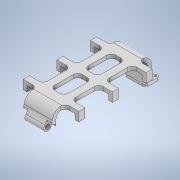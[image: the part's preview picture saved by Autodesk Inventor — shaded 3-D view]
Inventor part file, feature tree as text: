
AUTODESK INVENTOR PART (.ipt)
format: ipt  version: 2022 (Build 260153000, 153)  size: 560,640 bytes
history: native  units: mm
features: sketch x18, extrude x17, mirror x7, fillet x2, pattern_linear x1
ambient origin geometry x8: Origin, YZ Plane, XZ Plane, XY Plane, X Axis, Y Axis, Z Axis, Center Point
bodies: Solid1 (feature_tree)
feature tree (45):
  extrude  "Extrusion1"  Depth=15.4mm
  extrude  "Extrusion2"  Depth=1.5mm
  extrude  "Extrusion3"  Depth=6.0mm
  mirror  "Mirror1"
  mirror  "Mirror2"
  extrude  "Extrusion4"  Depth=1.0mm
  extrude  "Extrusion5"  Depth=3.0mm
  extrude  "Extrusion6"  Depth=16.0mm
  extrude  "Extrusion7"  Depth=3.0mm
  extrude  "Extrusion8"  Depth=1.0mm
  extrude  "Extrusion9"  Depth=1.0mm TaperAngle=0.0deg
  mirror  "Mirror4"
  extrude  "Extrusion11"  Depth=4.0mm TaperAngle=0.0deg
  extrude  "Extrusion12"  Depth=3.0mm
  mirror  "Mirror5"
  mirror  "Mirror6"
  pattern_linear  "Rectangular Pattern1"  Spacing1=2.0mm  [1 undecoded]
  extrude  "Extrusion13"  Depth=1.0mm
  extrude  "Extrusion14"  Depth=1.0mm
  extrude  "Extrusion15"  Depth=1.0mm
  mirror  "Mirror7"
  sketch  "Sketch16"  dims[d38=6.0mm]
  extrude  "Extrusion16"  Depth=1.0mm
  extrude  "Extrusion17"  TaperAngle=0.0deg  [1 undecoded]
  extrude  "Extrusion18"  Depth=2.5mm
  mirror  "Mirror8"
  fillet  "Fillet1"  Radius=12.5mm
  fillet  "Fillet2"  Radius=15.0mm
  sketch  "Sketch1"  dims[d0=36.5mm d1=15.4mm d2=7.7mm]
  sketch  "Sketch2"  dims[d5=1.5mm d9=1.5mm]
  sketch  "Sketch4"  dims[d12=2.0mm d13=6.0mm]
  sketch  "Sketch5"  dims[d14=1.0mm d15=1.0mm]
  sketch  "Sketch6"  dims[d16=2.5mm d17=3.0mm]
  sketch  "Sketch7"  dims[d20=9.5mm d21=16.0mm]
  sketch  "Sketch8"  dims[d22=0.0mm d23=3.0mm]
  sketch  "Sketch9"  dims[d24=3.0mm d25=1.0mm]
  sketch  "Sketch10"  dims[d26=1.0mm d27=2.0mm d28=0.0mm]
  sketch  "Sketch11"  dims[d29=2.0mm d30=4.0mm d31=0.0mm]
  sketch  "Sketch12"  dims[d32=6.5mm d33=3.0mm]
  sketch  "Sketch13"  dims[d34=2.0mm]
  sketch  "Sketch14"  dims[d35=2.0mm]
  sketch  "Sketch15"  dims[d36=2.0mm d37=0.0mm]
  sketch  "Sketch17"  dims[d41=3.0mm]
  sketch  "Sketch18"  dims[d42=3.0mm]
  sketch  "Sketch19"  dims[d43=3.0mm d44=2.0mm d45=0.0mm d46=60.0mm d47=30.5mm d48=15.25mm d49=30.0mm d50=0.0mm d51=0.0mm d52=2.5mm d53=12.5mm d54=0.0mm d55=15.0mm d56=7.5mm d57=3.75mm d58=12.5mm d59=0.0mm d60=0.0mm d61=0.0mm d62=9.0mm d63=20.0mm d64=4.7mm d65=10.0mm d66=0.0mm d67=2.0mm d68=3.0mm d69=3.0mm d70=3.0mm d75=6.5mm d76=2.0mm d77=2.5mm d78=0.0mm d79=6.0mm d80=3.0mm d83=6.0mm d84=2.5mm d85=0.0mm d86=30.0mm d88=22.0mm d89=0.0mm d90=0.0mm d91=0.0mm d92=0.0mm d93=10.0mm d94=0.0mm d95=5.0mm d96=3.0mm d97=7.0mm d98=2.5mm d99=0.0mm d100=0.0mm d101=10.0mm d102=0.0mm d103=5.2mm d104=3.0mm d105=0.0mm d106=5.5mm d107=1.0mm]
note: 2 required parameter values undecoded (feature->parameter linkage not recoverable at this tier; creation-order binding heuristic only, values carry confidence <= 0.55)
